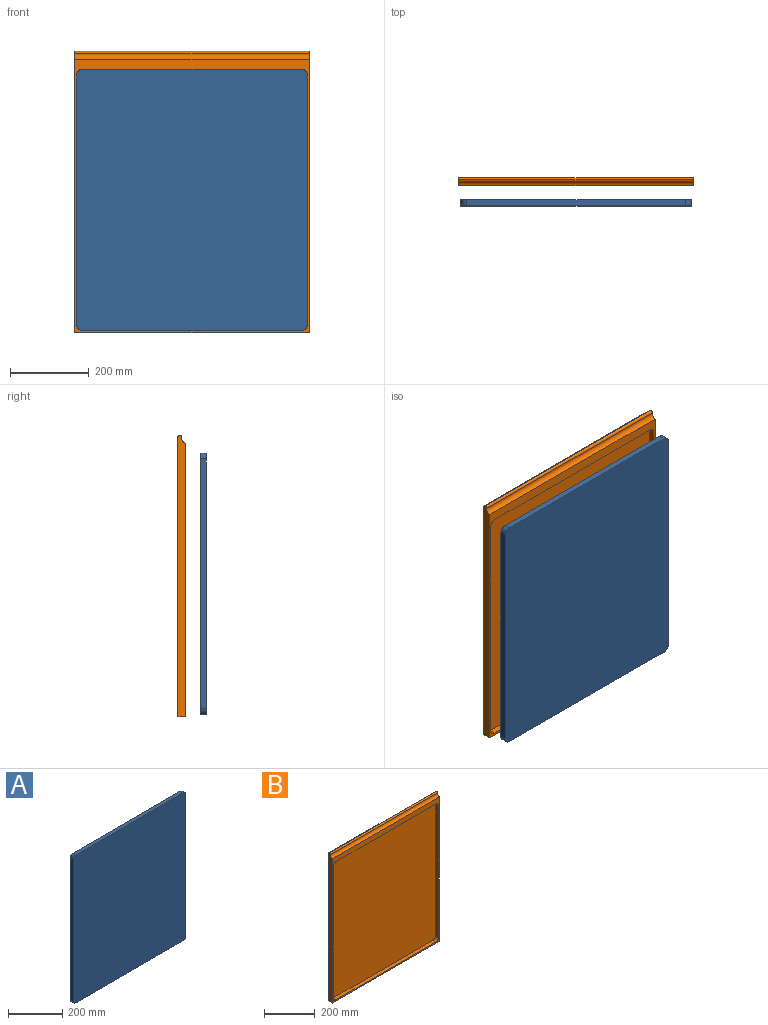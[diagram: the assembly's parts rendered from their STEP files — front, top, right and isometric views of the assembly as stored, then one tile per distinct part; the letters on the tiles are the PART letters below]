
ASSEMBLY  parts=2 mates=2
PART A: 10 faces, bbox 586x15.5x665 mm
  f0: plane 635x15.5mm, normal (1,0,0), area 9842.5mm2, adj f1,f7,f8,f9
  f1: cylinder r=15mm len=15.5mm, axis (0,1,0), area 365.2mm2, adj f0,f2,f8,f9
  f2: plane 556x15.5mm, normal (0,0,1), area 8618mm2, adj f1,f3,f8,f9
  f3: cylinder r=15mm len=15.5mm, axis (0,1,0), area 365.2mm2, adj f2,f4,f8,f9
  f4: plane 635x15.5mm, normal (-1,0,0), area 9842.5mm2, adj f3,f5,f8,f9
  f5: cylinder r=15mm len=15.5mm, axis (0,1,0), area 365.2mm2, adj f4,f6,f8,f9
  f6: plane 556x15.5mm, normal (0,0,-1), area 8618mm2, adj f5,f7,f8,f9
  f7: cylinder r=15mm len=15.5mm, axis (0,1,0), area 365.2mm2, adj f0,f6,f8,f9
  f8: plane 665x586mm, normal (0,-1,0), area 389496.9mm2, adj f0,f1,f2,f3,f4,f5,f6,f7
  f9: plane 665x586mm, normal (0,1,0), area 389496.9mm2, adj f0,f1,f2,f3,f4,f5,f6,f7
PART B: 17 faces, bbox 596x20x715 mm
  f0: plane 695x596mm, normal (0,-1,0), area 24723.1mm2, adj f1,f2,f4,f5,f6,f7,f8,f10
  f1: plane 715x20mm, normal (-1,0,0), area 14119mm2, adj f0,f3,f4,f14,f15,f16
  f2: plane 715x20mm, normal (1,0,0), area 14119mm2, adj f0,f3,f4,f14,f15,f16
  f3: plane 710x596mm, normal (0,1,0), area 423160mm2, adj f1,f2,f4,f14
  f4: plane 596x20mm, normal (0,0,-1), area 11920mm2, adj f0,f1,f2,f3
  f5: plane 635x16.5mm, normal (1,0,0), area 10477.5mm2, adj f0,f9,f10,f13
  f6: plane 556x16.5mm, normal (0,0,1), area 9174mm2, adj f0,f9,f10,f11
  f7: plane 635x16.5mm, normal (-1,0,0), area 10477.5mm2, adj f0,f9,f11,f12
  f8: plane 556x16.5mm, normal (0,0,-1), area 9174mm2, adj f0,f9,f12,f13
  f9: plane 665x586mm, normal (0,-1,0), area 389496.9mm2, adj f5,f6,f7,f8,f10,f11,f12,f13
  f10: cylinder r=15mm len=16.5mm, axis (0,-1,0), area 388.8mm2, adj f0,f5,f6,f9
  f11: cylinder r=15mm len=16.5mm, axis (0,1,0), area 388.8mm2, adj f0,f6,f7,f9
  f12: cylinder r=15mm len=16.5mm, axis (0,-1,0), area 388.8mm2, adj f0,f7,f8,f9
  f13: cylinder r=15mm len=16.5mm, axis (0,1,0), area 388.8mm2, adj f0,f5,f8,f9
  f14: cylinder r=5mm len=596mm, axis (-1,0,0), area 4681mm2, adj f1,f2,f3,f15
  f15: cylinder r=5.06mm len=596mm, axis (-1,0,0), area 5178.2mm2, adj f1,f2,f14,f16
  f16: cylinder r=12.59mm len=596mm, axis (-1,0,0), area 11423.5mm2, adj f0,f1,f2,f15
PLACE A t=(5,-36.5,5)mm
PLACE B t=(0,20,0)mm
MATE planar A.f4 <-> B.f5  axis (-1,0,0) through (5,-44.25,337.5)mm
MATE planar B.f8 <-> A.f2  axis (0,0,-1) through (298,8.25,670)mm
